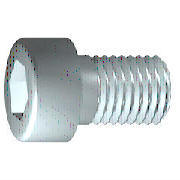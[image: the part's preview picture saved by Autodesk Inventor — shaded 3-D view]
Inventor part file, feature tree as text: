
AUTODESK INVENTOR PART (.ipt)
format: ipt  version: 2019 (Build 230136000, 136)  size: 193,024 bytes
history: native  units: mm (DEFAULTED — no unit token found)
features: sketch x2, extrude x1, plane x1, fillet x1
ambient origin geometry x7: Origin, YZ Plane, XY Plane, X Axis, Y Axis, Z Axis, Center Point
bodies: Solid1 (feature_tree), Body (feature_tree)
feature tree (5):
  extrude  "Slot"  Depth=3.0mm
  plane  "Work Plane1"
  fillet  "Fillet2"  Radius=3.0mm
  sketch  "Sketch1"  dims[d1=4.75mm d2=0.306825mm d3=3.0mm]
  sketch  "Sketch2"  dims[d4=1.3mm d5=60.0deg d6=3.0mm d7=3.0mm d8=2.886751mm d9=5.5mm d10=90.0deg d11=10.0mm d12=0.0mm d13=4.75mm d14=0.0mm d15=0.306725mm d16=0.306725mm d17=0.3mm d19=0.0mm d26=6.0mm d27=45.0deg d28=0.0mm d29=0.0mm d30=0.1mm]
